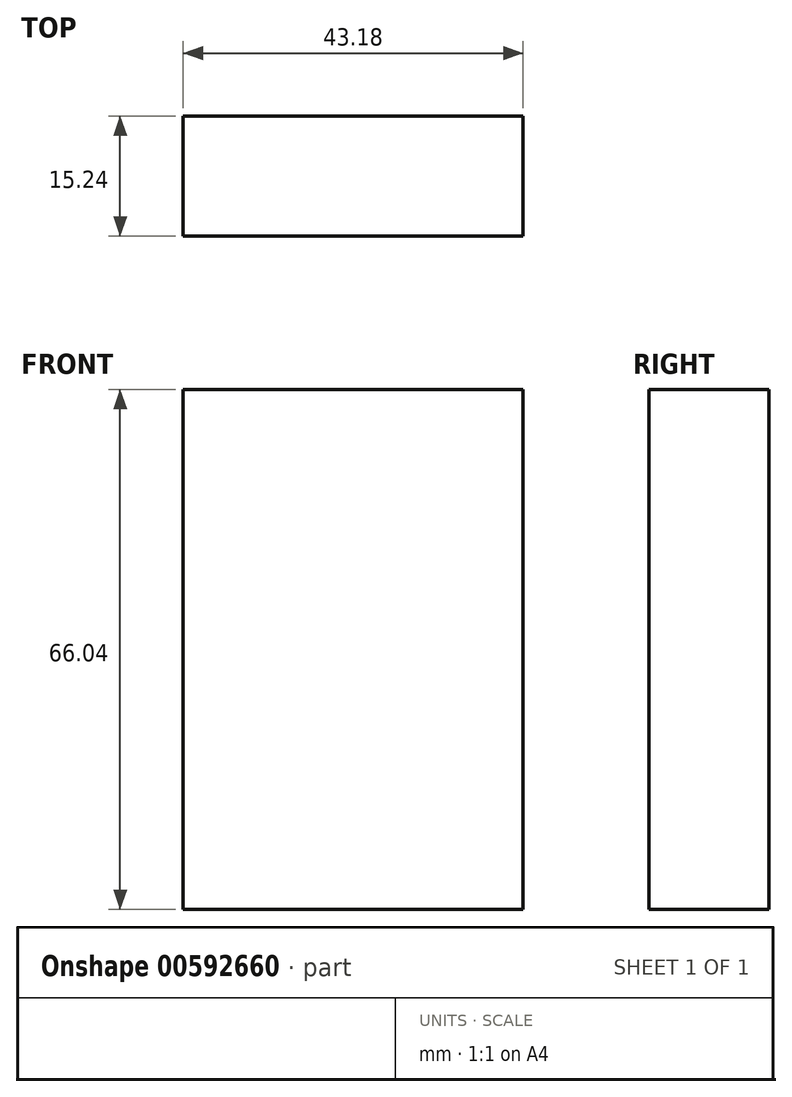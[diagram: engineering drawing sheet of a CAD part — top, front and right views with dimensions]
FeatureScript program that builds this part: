
annotation { "Feature Type Name" : "Feature", "Feature Type Description" : "" }
export const myFeature = defineFeature(function(context is Context, id is Id, definition is map)
    precondition{}
    {
        {
            var Q0;
            Q0=qCreatedBy(makeId("Front.planeOp"),FACE);
            var sketch = newSketch(context, id + "F0", { "sketchPlane" : qUnion([Q0])});
            skLineSegment(sketch, "E0.bottom", {"start": v(21.6, -12.7) * mm, "end": v(-21.59, -12.7) * mm});
            skLineSegment(sketch, "E0.top", {"start": v(21.6, 12.7) * mm, "end": v(-21.59, 12.7) * mm});
            skLineSegment(sketch, "E0.left", {"start": v(21.6, -12.7) * mm, "end": v(21.6, 12.7) * mm});
            skLineSegment(sketch, "E0.right", {"start": v(-21.59, -12.7) * mm, "end": v(-21.59, 12.7) * mm});
            skPoint(sketch, "E0.middle", {"position": v(0, 0) * mm});
            skLineSegment(sketch, "E1.bottom", {"start": v(21.6, 33.02) * mm, "end": v(-21.59, 33.02) * mm});
            skLineSegment(sketch, "E1.top", {"start": v(21.6, 53.34) * mm, "end": v(-21.59, 53.34) * mm});
            skLineSegment(sketch, "E1.left", {"start": v(21.59, 33.02) * mm, "end": v(21.59, 53.34) * mm});
            skLineSegment(sketch, "E1.right", {"start": v(-21.59, 33.02) * mm, "end": v(-21.59, 53.34) * mm});
            skPoint(sketch, "E1.middle", {"position": v(0, 43.18) * mm});
            skLineSegment(sketch, "E2", {"start": v(-21.59, 33.02) * mm, "end": v(-21.59, 12.7) * mm});
            skLineSegment(sketch, "E3", {"start": v(21.6, 33.02) * mm, "end": v(21.6, 12.7) * mm});
            skSolve(sketch);
        }
        {
            var Q0;
            Q0=makeQuery(id+"F0.imprint","IMPRINT",FACE,{"disambiguationData":[TD([[makeQuery(id+"F0.imprint","IMPRINT",EDGE,{"derivedFrom":sQuery(id+"F0.wireOp",EDGE,"E0.bottom")}),-1.0]])]});
            var Q1;
            Q1=makeQuery(id+"F0.imprint","IMPRINT",FACE,{"disambiguationData":[TD([[makeQuery(id+"F0.imprint","IMPRINT",EDGE,{"derivedFrom":sQuery(id+"F0.wireOp",EDGE,"E0.top")}),-1.0]])]});
            var Q2;
            Q2=makeQuery(id+"F0.imprint","IMPRINT",FACE,{"disambiguationData":[TD([[makeQuery(id+"F0.imprint","IMPRINT",EDGE,{"derivedFrom":sQuery(id+"F0.wireOp",EDGE,"E1.bottom")}),-1.0]])]});
            extrude(context, id + "F1", {"entities" : qUnion([Q0, Q1, Q2]), "depth" : 15.24 * mm, "offsetDistance" : 25.4 * mm});
        }
    });
